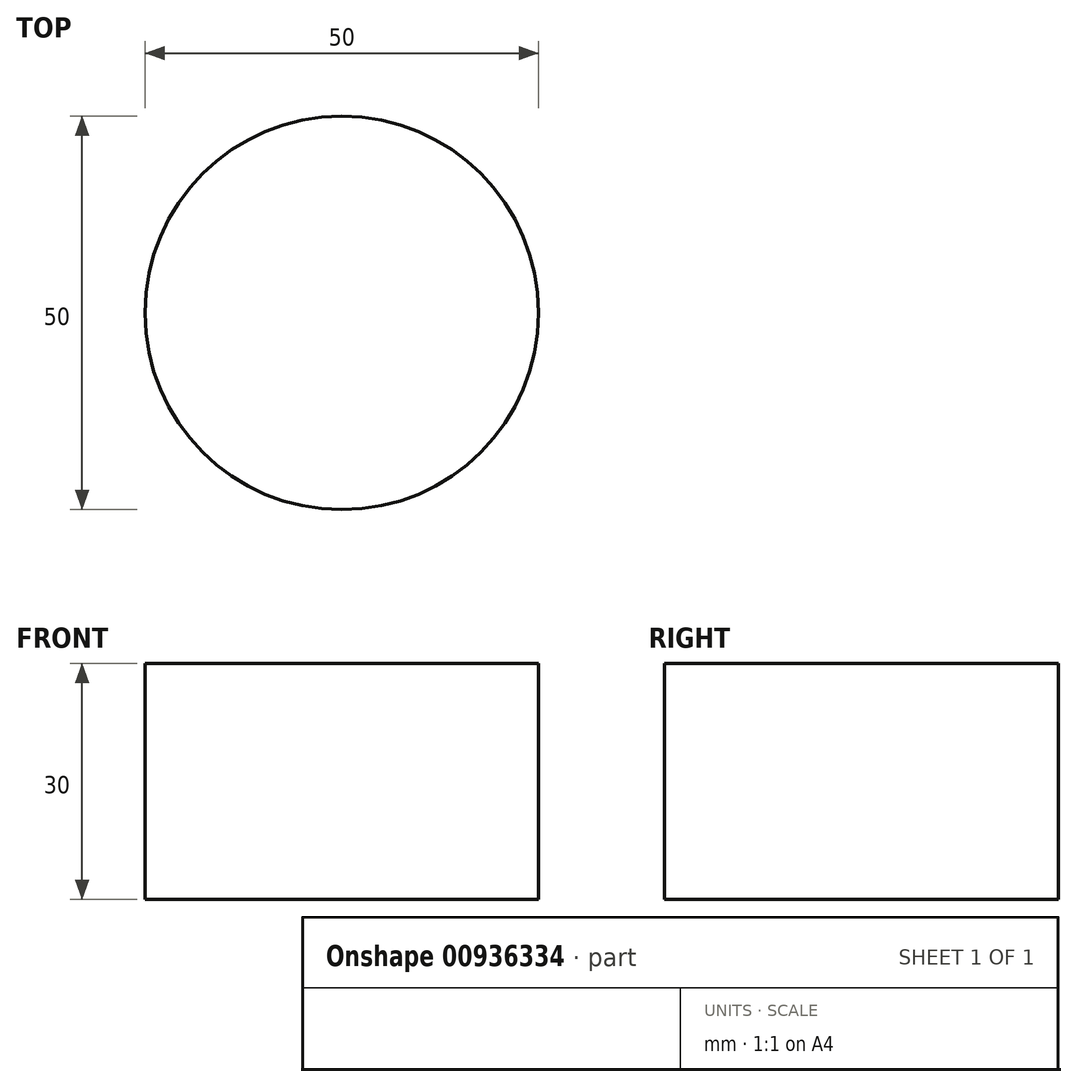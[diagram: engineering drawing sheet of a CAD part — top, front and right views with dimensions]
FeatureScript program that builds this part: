
annotation { "Feature Type Name" : "Feature", "Feature Type Description" : "" }
export const myFeature = defineFeature(function(context is Context, id is Id, definition is map)
    precondition{}
    {
        {
            var Q0;
            Q0=qCreatedBy(makeId("Right.planeOp"),FACE);
            var sketch = newSketch(context, id + "F0", { "sketchPlane" : qUnion([Q0])});
            skLineSegment(sketch, "E0.bottom", {"start": v(0, 0) * mm, "end": v(25, 0) * mm});
            skLineSegment(sketch, "E0.top", {"start": v(0, 30) * mm, "end": v(25, 30) * mm});
            skLineSegment(sketch, "E0.left", {"start": v(0, 0) * mm, "end": v(0, 30) * mm});
            skLineSegment(sketch, "E0.right", {"start": v(25, 0) * mm, "end": v(25, 30) * mm});
            skSolve(sketch);
        }
        {
            var Q0;
            Q0=qSketchRegion(id+"F0",true);
            var Q1;
            Q1=sQuery(id+"F0.wireOp",EDGE,"E0.left");
            revolve(context, id + "F1", {"surfaceOperationType" : NewSurfaceOperationType.NEW, "entities" : qUnion([Q0]), "axis" : qUnion([Q1]), "revolveType" : RevolveType.FULL});
        }
    });
